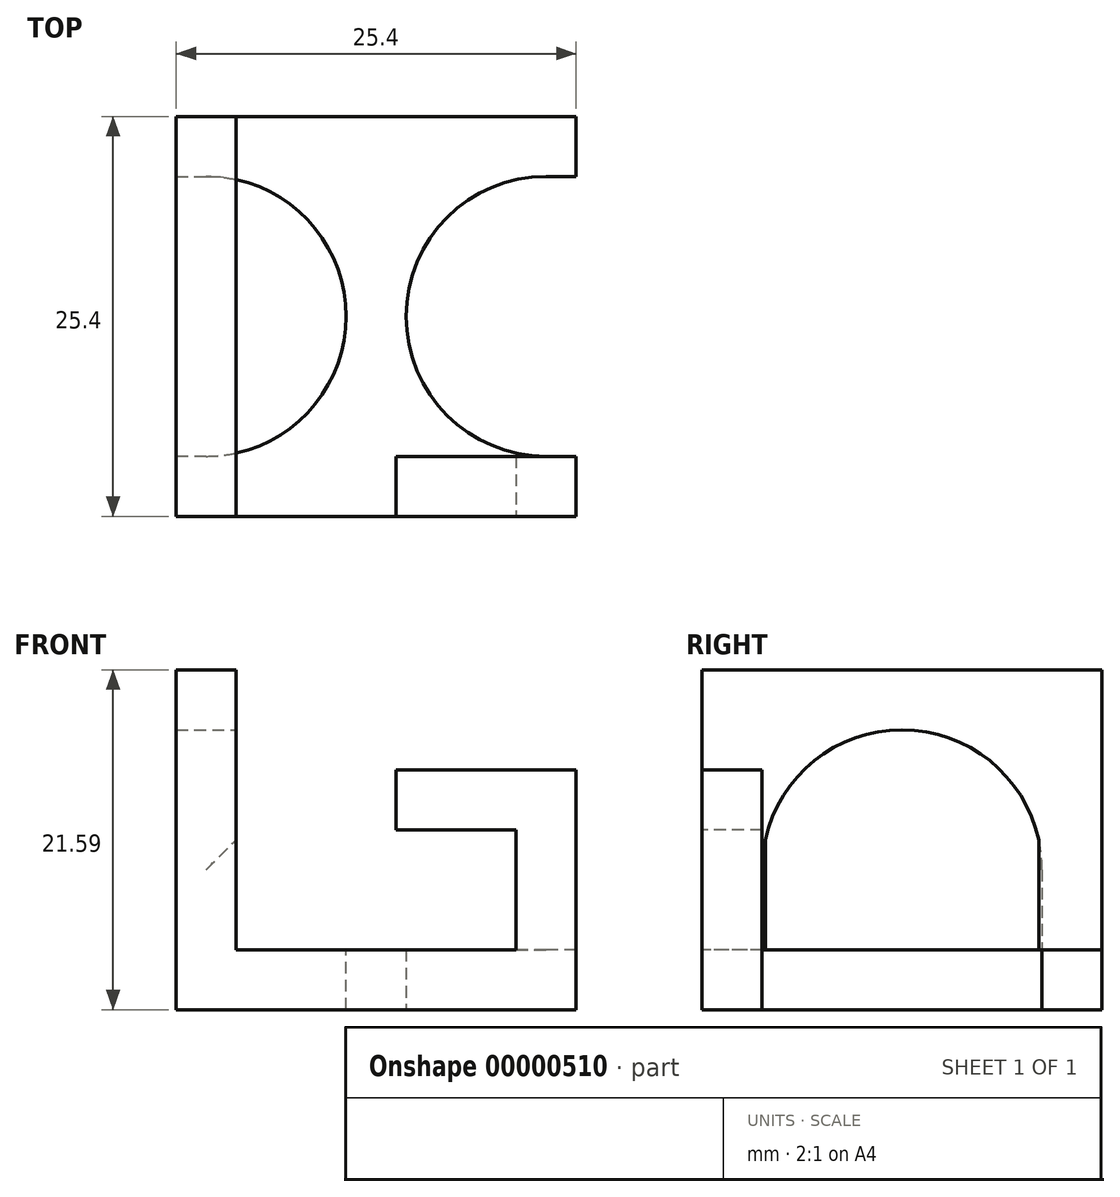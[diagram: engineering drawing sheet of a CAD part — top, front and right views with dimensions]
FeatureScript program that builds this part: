
annotation { "Feature Type Name" : "Feature", "Feature Type Description" : "" }
export const myFeature = defineFeature(function(context is Context, id is Id, definition is map)
    precondition{}
    {
        {
            var Q0;
            Q0=qCreatedBy(makeId("Top.planeOp"),FACE);
            var sketch = newSketch(context, id + "F0", { "sketchPlane" : qUnion([Q0])});
            skLineSegment(sketch, "E0.rect.bottom", {"start": v(-1.9, -8.89) * mm, "end": v(1.9, -8.89) * mm});
            skLineSegment(sketch, "E0.rect.top", {"start": v(-1.9, 8.9) * mm, "end": v(1.9, 8.9) * mm});
            skLineSegment(sketch, "E0.rect.left", {"start": v(-1.9, -8.89) * mm, "end": v(-1.9, 8.9) * mm});
            skLineSegment(sketch, "E0.rect.right", {"start": v(1.9, -8.89) * mm, "end": v(1.9, 8.89) * mm});
            skPoint(sketch, "E0.rect.middle", {"position": v(0, 0) * mm});
            skLineSegment(sketch, "E1.bottom", {"start": v(-12.7, -8.89) * mm, "end": v(12.7, -8.89) * mm});
            skLineSegment(sketch, "E1.top", {"start": v(-12.7, -12.7) * mm, "end": v(12.7, -12.7) * mm});
            skLineSegment(sketch, "E1.left", {"start": v(-12.7, -8.89) * mm, "end": v(-12.7, -12.7) * mm});
            skLineSegment(sketch, "E1.right", {"start": v(12.7, -8.89) * mm, "end": v(12.7, -12.7) * mm});
            skLineSegment(sketch, "E2.bottom", {"start": v(12.7, 8.9) * mm, "end": v(-12.7, 8.89) * mm});
            skLineSegment(sketch, "E2.top", {"start": v(12.7, 12.7) * mm, "end": v(-12.7, 12.7) * mm});
            skLineSegment(sketch, "E2.left", {"start": v(12.7, 8.89) * mm, "end": v(12.7, 12.7) * mm});
            skLineSegment(sketch, "E2.right", {"start": v(-12.7, 8.89) * mm, "end": v(-12.7, 12.7) * mm});
            skLineSegment(sketch, "E3", {"start": v(-12.7, 8.9) * mm, "end": v(-1.9, 8.9) * mm});
            skLineSegment(sketch, "E4", {"start": v(1.9, 8.89) * mm, "end": v(12.7, 8.9) * mm});
            skLineSegment(sketch, "E5", {"start": v(12.7, -8.9) * mm, "end": v(1.9, -8.9) * mm});
            skLineSegment(sketch, "E6", {"start": v(-1.9, -8.9) * mm, "end": v(-12.7, -8.9) * mm});
            skLineSegment(sketch, "E7", {"start": v(1.9, 8.9) * mm, "end": v(12.7, 8.9) * mm});
            skSolve(sketch);
        }
        {
            var Q0;
            Q0 = qSketchRegion(id + "F0", true);
            extrude(context, id + "F1", {"entities" : qUnion([Q0]), "depth" : 3.8 * mm});
        }
        {
            var Q0;
            Q0=makeQuery(id+"F1.opExtrude","CAP_FACE",FACE,{"disambiguationData":[OSD([sQuery(id+"F0.wireOp",EDGE,"E0.rect.left"),sQuery(id+"F0.wireOp",EDGE,"E0.rect.right"),sQuery(id+"F0.wireOp",EDGE,"E1.top"),sQuery(id+"F0.wireOp",EDGE,"E1.left"),sQuery(id+"F0.wireOp",EDGE,"E1.right"),sQuery(id+"F0.wireOp",EDGE,"E2.top"),sQuery(id+"F0.wireOp",EDGE,"E2.left"),sQuery(id+"F0.wireOp",EDGE,"E2.right"),sQuery(id+"F0.wireOp",EDGE,"E3"),sQuery(id+"F0.wireOp",EDGE,"E5"),sQuery(id+"F0.wireOp",EDGE,"E6"),sQuery(id+"F0.wireOp",EDGE,"E7")])],"isStart":false});
            var sketch = newSketch(context, id + "F2", { "sketchPlane" : qUnion([Q0])});
            skLineSegment(sketch, "E8.bottom", {"start": v(-12.7, -8.9) * mm, "end": v(-8.89, -8.9) * mm});
            skLineSegment(sketch, "E8.top", {"start": v(-12.7, -12.7) * mm, "end": v(-8.89, -12.7) * mm});
            skLineSegment(sketch, "E8.left", {"start": v(-12.7, -8.9) * mm, "end": v(-12.7, -12.7) * mm});
            skLineSegment(sketch, "E8.right", {"start": v(-8.89, -8.9) * mm, "end": v(-8.89, -12.7) * mm});
            skSolve(sketch);
        }
        {
            var Q0;
            Q0 = qSketchRegion(id + "F2", true);
            extrude(context, id + "F3", {"entities" : qUnion([Q0]), "operationType" : NewBodyOperationType.ADD, "depth" : 17.78 * mm});
        }
        {
            var Q0;
            Q0=makeQuery(id+"F1.opExtrude","CAP_FACE",FACE,{"disambiguationData":[OSD([sQuery(id+"F0.wireOp",EDGE,"E0.rect.left"),sQuery(id+"F0.wireOp",EDGE,"E0.rect.right"),sQuery(id+"F0.wireOp",EDGE,"E1.top"),sQuery(id+"F0.wireOp",EDGE,"E1.left"),sQuery(id+"F0.wireOp",EDGE,"E1.right"),sQuery(id+"F0.wireOp",EDGE,"E2.top"),sQuery(id+"F0.wireOp",EDGE,"E2.left"),sQuery(id+"F0.wireOp",EDGE,"E2.right"),sQuery(id+"F0.wireOp",EDGE,"E3"),sQuery(id+"F0.wireOp",EDGE,"E5"),sQuery(id+"F0.wireOp",EDGE,"E6"),sQuery(id+"F0.wireOp",EDGE,"E7")])],"isStart":false});
            var sketch = newSketch(context, id + "F4", { "sketchPlane" : qUnion([Q0])});
            skLineSegment(sketch, "E9.bottom", {"start": v(12.7, -8.9) * mm, "end": v(8.9, -8.9) * mm});
            skLineSegment(sketch, "E9.top", {"start": v(12.7, -12.7) * mm, "end": v(8.9, -12.7) * mm});
            skLineSegment(sketch, "E9.left", {"start": v(12.7, -8.9) * mm, "end": v(12.7, -12.7) * mm});
            skLineSegment(sketch, "E9.right", {"start": v(8.9, -8.9) * mm, "end": v(8.9, -12.7) * mm});
            skSolve(sketch);
        }
        {
            var Q0;
            Q0 = qSketchRegion(id + "F4", true);
            extrude(context, id + "F5", {"entities" : qUnion([Q0]), "operationType" : NewBodyOperationType.ADD, "depth" : 11.43 * mm});
        }
        {
            var Q0;
            Q0=makeQuery(id+"F5.opExtrude","SWEPT_FACE",FACE,{"disambiguationData":[OSD([sQuery(id+"F4.wireOp",EDGE,"E9.right")])]});
            var sketch = newSketch(context, id + "F6", { "sketchPlane" : qUnion([Q0])});
            skLineSegment(sketch, "E10.bottom", {"start": v(8.9, 15.24) * mm, "end": v(12.7, 15.24) * mm});
            skLineSegment(sketch, "E10.top", {"start": v(8.9, 11.43) * mm, "end": v(12.7, 11.43) * mm});
            skLineSegment(sketch, "E10.left", {"start": v(8.9, 15.24) * mm, "end": v(8.9, 11.43) * mm});
            skLineSegment(sketch, "E10.right", {"start": v(12.7, 15.24) * mm, "end": v(12.7, 11.43) * mm});
            skSolve(sketch);
        }
        {
            var Q0;
            Q0 = qSketchRegion(id + "F6", true);
            extrude(context, id + "F7", {"entities" : qUnion([Q0]), "operationType" : NewBodyOperationType.ADD, "depth" : 7.62 * mm});
        }
        {
            var Q0;
            Q0=makeQuery(id+"F1.opExtrude","CAP_FACE",FACE,{"disambiguationData":[OSD([sQuery(id+"F0.wireOp",EDGE,"E0.rect.left"),sQuery(id+"F0.wireOp",EDGE,"E0.rect.right"),sQuery(id+"F0.wireOp",EDGE,"E1.top"),sQuery(id+"F0.wireOp",EDGE,"E1.left"),sQuery(id+"F0.wireOp",EDGE,"E1.right"),sQuery(id+"F0.wireOp",EDGE,"E2.top"),sQuery(id+"F0.wireOp",EDGE,"E2.left"),sQuery(id+"F0.wireOp",EDGE,"E2.right"),sQuery(id+"F0.wireOp",EDGE,"E3"),sQuery(id+"F0.wireOp",EDGE,"E5"),sQuery(id+"F0.wireOp",EDGE,"E6"),sQuery(id+"F0.wireOp",EDGE,"E7")])],"isStart":false});
            var sketch = newSketch(context, id + "F8", { "sketchPlane" : qUnion([Q0])});
            skLineSegment(sketch, "E11.bottom", {"start": v(-12.7, 8.9) * mm, "end": v(-8.89, 8.9) * mm});
            skLineSegment(sketch, "E11.top", {"start": v(-12.7, 12.7) * mm, "end": v(-8.89, 12.7) * mm});
            skLineSegment(sketch, "E11.left", {"start": v(-12.7, 8.9) * mm, "end": v(-12.7, 12.7) * mm});
            skLineSegment(sketch, "E11.right", {"start": v(-8.89, 8.9) * mm, "end": v(-8.89, 12.7) * mm});
            skSolve(sketch);
        }
        {
            var Q0;
            Q0 = qSketchRegion(id + "F8", true);
            extrude(context, id + "F9", {"entities" : qUnion([Q0]), "operationType" : NewBodyOperationType.ADD, "depth" : 17.78 * mm});
        }
        {
            var Q0;
            Q0=makeQuery(id+"F9.boolean.opBoolean","MERGE",FACE,{"derivedFrom":[makeQuery(id+"F1.opExtrude","SWEPT_FACE",FACE,{"disambiguationData":[OSD([sQuery(id+"F0.wireOp",EDGE,"E3")])]}),makeQuery(id+"F9.opExtrude","SWEPT_FACE",FACE,{"disambiguationData":[OSD([sQuery(id+"F8.wireOp",EDGE,"E11.bottom")])]})]});
            var sketch = newSketch(context, id + "F10", { "sketchPlane" : qUnion([Q0])});
            skLineSegment(sketch, "E12.bottom", {"start": v(-12.7, 21.59) * mm, "end": v(-8.89, 21.59) * mm});
            skLineSegment(sketch, "E12.top", {"start": v(-12.7, 17.78) * mm, "end": v(-8.89, 17.78) * mm});
            skLineSegment(sketch, "E12.left", {"start": v(-12.7, 21.59) * mm, "end": v(-12.7, 17.78) * mm});
            skLineSegment(sketch, "E12.right", {"start": v(-8.89, 21.59) * mm, "end": v(-8.89, 17.78) * mm});
            skSolve(sketch);
        }
        {
            var Q0;
            Q0 = qSketchRegion(id + "F10", true);
            var Q1;
            Q1=makeQuery(id+"F3.boolean.opBoolean","MERGE",FACE,{"derivedFrom":[makeQuery(id+"F1.opExtrude","SWEPT_FACE",FACE,{"disambiguationData":[OSD([sQuery(id+"F0.wireOp",EDGE,"E6")])]}),makeQuery(id+"F3.opExtrude","SWEPT_FACE",FACE,{"disambiguationData":[OSD([sQuery(id+"F2.wireOp",EDGE,"E8.bottom")])]})]});
            extrude(context, id + "F11", {"entities" : qUnion([Q0]), "operationType" : NewBodyOperationType.ADD, "endBound" : BoundingType.UP_TO_SURFACE, "endBoundEntityFace" : qUnion([Q1]), "depth" : 25.4 * mm});
        }
        {
            var Q0;
            Q0=makeQuery(id+"F1.opExtrude","SWEPT_EDGE",EDGE,{"disambiguationData":[OSD([sQuery(id+"F0.wireOp",EDGE,"E0.rect.right"),sQuery(id+"F0.wireOp",EDGE,"E2.bottom"),sQuery(id+"F0.wireOp",EDGE,"E7")])]});
            var Q1;
            Q1=makeQuery(id+"F1.opExtrude","SWEPT_EDGE",EDGE,{"disambiguationData":[OSD([sQuery(id+"F0.wireOp",EDGE,"E0.rect.right"),sQuery(id+"F0.wireOp",EDGE,"E5"),sQuery(id+"F0.wireOp",EDGE,"E0.rect.bottom")])]});
            var Q2;
            Q2=makeQuery(id+"F1.opExtrude","SWEPT_EDGE",EDGE,{"disambiguationData":[OSD([sQuery(id+"F0.wireOp",EDGE,"E0.rect.left"),sQuery(id+"F0.wireOp",EDGE,"E6"),sQuery(id+"F0.wireOp",EDGE,"E0.rect.bottom")])]});
            var Q3;
            Q3=makeQuery(id+"F1.opExtrude","SWEPT_EDGE",EDGE,{"disambiguationData":[OSD([sQuery(id+"F0.wireOp",EDGE,"E0.rect.left"),sQuery(id+"F0.wireOp",EDGE,"E2.bottom"),sQuery(id+"F0.wireOp",EDGE,"E3")])]});
            fillet(context, id + "F12", {"entities" : qUnion([Q0, Q1, Q2, Q3]), "radius" : 8.9 * mm, "tangentPropagation" : true, "allowEdgeOverflow" : false});
        }
        {
            var Q0;
            Q0=makeQuery(id+"F12.opFillet","BLEND_EDGE",EDGE,{"blendedFrom":[makeQuery(id+"F1.opExtrude","SWEPT_EDGE",EDGE,{"disambiguationData":[OSD([sQuery(id+"F0.wireOp",EDGE,"E0.rect.left"),sQuery(id+"F0.wireOp",EDGE,"E2.bottom"),sQuery(id+"F0.wireOp",EDGE,"E3")])]}),makeQuery(id+"F11.opExtrude","SWEPT_FACE",FACE,{"disambiguationData":[OSD([sQuery(id+"F10.wireOp",EDGE,"E12.top")])]})],"blendedInto":[makeQuery(id+"F11.opExtrude","SWEPT_FACE",FACE,{"disambiguationData":[OSD([sQuery(id+"F10.wireOp",EDGE,"E12.top")])]})]});
            var Q1;
            Q1=makeQuery(id+"F11.opExtrude","CAP_EDGE",EDGE,{"disambiguationData":[OSD([sQuery(id+"F10.wireOp",EDGE,"E12.top")])],"isStart":true});
            var Q2;
            Q2=makeQuery(id+"F12.opFillet","BLEND_EDGE",EDGE,{"blendedFrom":[makeQuery(id+"F1.opExtrude","SWEPT_EDGE",EDGE,{"disambiguationData":[OSD([sQuery(id+"F0.wireOp",EDGE,"E0.rect.left"),sQuery(id+"F0.wireOp",EDGE,"E6"),sQuery(id+"F0.wireOp",EDGE,"E0.rect.bottom")])]}),makeQuery(id+"F11.opExtrude","SWEPT_FACE",FACE,{"disambiguationData":[OSD([sQuery(id+"F10.wireOp",EDGE,"E12.top")])]})],"blendedInto":[makeQuery(id+"F11.opExtrude","SWEPT_FACE",FACE,{"disambiguationData":[OSD([sQuery(id+"F10.wireOp",EDGE,"E12.top")])]})]});
            var Q3;
            Q3=makeQuery(id+"F11.opExtrude","CAP_EDGE",EDGE,{"disambiguationData":[OSD([sQuery(id+"F10.wireOp",EDGE,"E12.top")])],"isStart":false});
            fillet(context, id + "F13", {"entities" : qUnion([Q0, Q1, Q2, Q3]), "radius" : 8.9 * mm, "tangentPropagation" : true, "allowEdgeOverflow" : false});
        }
    });
